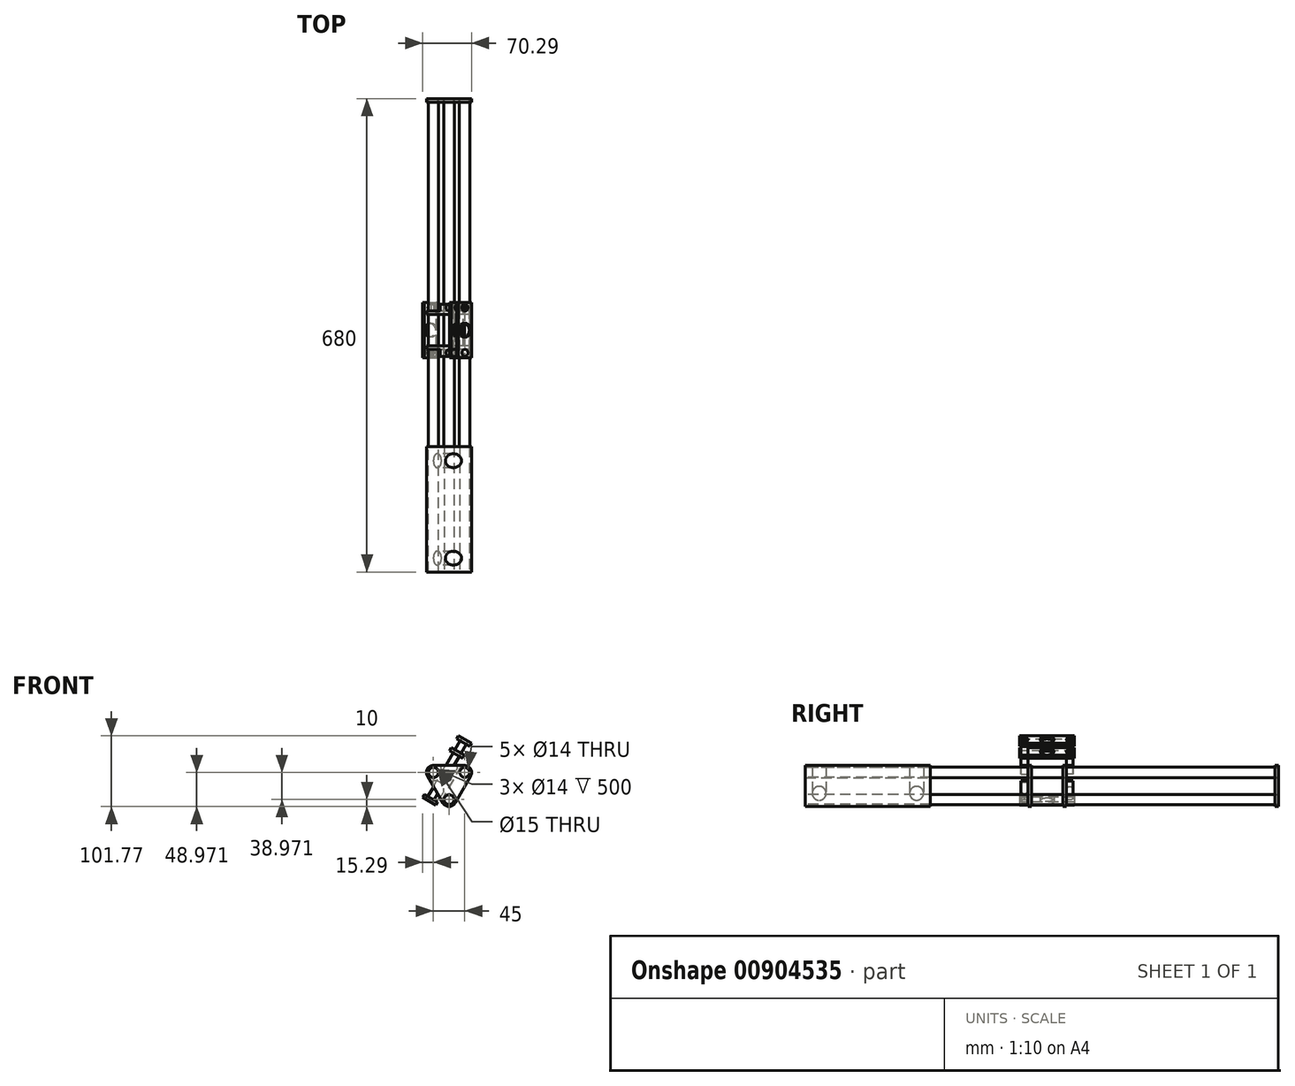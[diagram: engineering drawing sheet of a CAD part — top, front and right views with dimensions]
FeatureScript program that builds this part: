
annotation { "Feature Type Name" : "Feature", "Feature Type Description" : "" }
export const myFeature = defineFeature(function(context is Context, id is Id, definition is map)
    precondition{}
    {
        {
            var Q0;
            Q0=qCreatedBy(makeId("Front.planeOp"),FACE);
            var sketch = newSketch(context, id + "F0", { "sketchPlane" : qUnion([Q0])});
            skCircle(sketch, "E0", {"center": v(-22.5, 38.97) * mm, "radius": 7.5 * mm});
            skCircle(sketch, "E1", {"center": v(22.5, 38.97) * mm, "radius": 7.5 * mm});
            skCircle(sketch, "E2", {"center": v(0, 0) * mm, "radius": 7.5 * mm});
            skCircle(sketch, "E3", {"center": v(-22.5, 38.97) * mm, "radius": 7 * mm});
            skCircle(sketch, "E4", {"center": v(22.5, 38.97) * mm, "radius": 7 * mm});
            skCircle(sketch, "E5", {"center": v(0, 0) * mm, "radius": 7 * mm});
            skSolve(sketch);
        }
        {
            var Q0;
            Q0=makeQuery(id+"F0.imprint","IMPRINT",FACE,{"disambiguationData":[TD([[makeQuery(id+"F0.imprint","IMPRINT",EDGE,{"derivedFrom":sQuery(id+"F0.wireOp",EDGE,"E0")}),1.0]])]});
            var Q1;
            Q1=makeQuery(id+"F0.imprint","IMPRINT",FACE,{"disambiguationData":[TD([[makeQuery(id+"F0.imprint","IMPRINT",EDGE,{"derivedFrom":sQuery(id+"F0.wireOp",EDGE,"E1")}),1.0]])]});
            var Q2;
            Q2=makeQuery(id+"F0.imprint","IMPRINT",FACE,{"disambiguationData":[TD([[makeQuery(id+"F0.imprint","IMPRINT",EDGE,{"derivedFrom":sQuery(id+"F0.wireOp",EDGE,"E2")}),1.0]])]});
            extrude(context, id + "F1", {"entities" : qUnion([Q0, Q1, Q2]), "depth" : 500 * mm, "offsetDistance" : 25 * mm});
        }
        {
            var Q0;
            Q0=qCreatedBy(makeId("Front.planeOp"),FACE);
            var sketch = newSketch(context, id + "F2", { "sketchPlane" : qUnion([Q0])});
            skLineSegment(sketch, "E6", {"start": v(22.5, 48.97) * mm, "end": v(-22.5, 48.97) * mm});
            skArc(sketch, "E7", {"start": v(-22.5, 48.97) * mm, "mid": v(-31.16, 43.97) * mm, "end": v(-31.16, 33.97) * mm});
            skArc(sketch, "E8", {"start": v(31.16, 33.97) * mm, "mid": v(31.16, 43.97) * mm, "end": v(22.5, 48.97) * mm});
            skLineSegment(sketch, "E9", {"start": v(31.16, 33.97) * mm, "end": v(8.66, -5) * mm});
            skArc(sketch, "E10", {"start": v(-8.66, -5) * mm, "mid": v(0, -10) * mm, "end": v(8.66, -5) * mm});
            skLineSegment(sketch, "E11", {"start": v(-31.16, 33.97) * mm, "end": v(-8.66, -5) * mm});
            skSolve(sketch);
        }
        {
            var Q0;
            Q0=makeQuery(id+"F2.imprint","IMPRINT",FACE,{"disambiguationData":[TD([[makeQuery(id+"F2.imprint","IMPRINT",EDGE,{"derivedFrom":sQuery(id+"F2.wireOp",EDGE,"E6")}),1.0]])]});
            extrude(context, id + "F3", {"entities" : qUnion([Q0]), "depth" : 5 * mm, "offsetDistance" : 25 * mm});
        }
        {
            var Q0;
            Q0=makeQuery(id+"F1.opExtrude","CAP_FACE",FACE,{"disambiguationData":[OSD([sQuery(id+"F0.wireOp",EDGE,"E0"),sQuery(id+"F0.wireOp",EDGE,"E3")])],"isStart":false});
            var sketch = newSketch(context, id + "F4", { "sketchPlane" : qUnion([Q0])});
            skLineSegment(sketch, "E12", {"start": v(-22.5, 48.97) * mm, "end": v(22.5, 48.97) * mm});
            skArc(sketch, "E13", {"start": v(-22.5, 48.97) * mm, "mid": v(-31.16, 43.97) * mm, "end": v(-31.16, 33.97) * mm});
            skArc(sketch, "E14", {"start": v(31.16, 33.97) * mm, "mid": v(31.16, 43.97) * mm, "end": v(22.5, 48.97) * mm});
            skArc(sketch, "E15", {"start": v(-8.66, -5) * mm, "mid": v(0, -10) * mm, "end": v(8.66, -5) * mm});
            skLineSegment(sketch, "E16", {"start": v(-31.16, 33.97) * mm, "end": v(-8.66, -5) * mm});
            skLineSegment(sketch, "E17", {"start": v(31.16, 33.97) * mm, "end": v(8.66, -5) * mm});
            skSolve(sketch);
        }
        {
            var Q0;
            Q0=makeQuery(id+"F4.imprint","IMPRINT",FACE,{"disambiguationData":[TD([[makeQuery(id+"F4.imprint","IMPRINT",EDGE,{"derivedFrom":sQuery(id+"F4.wireOp",EDGE,"E12")}),-1.0]])]});
            extrude(context, id + "F5", {"entities" : qUnion([Q0]), "depth" : 180 * mm, "offsetDistance" : 25 * mm});
        }
        {
            var Q0;
            Q0=makeQuery(id+"F5.opExtrude","SWEPT_EDGE",EDGE,{"disambiguationData":[OSD([sQuery(id+"F4.wireOp",EDGE,"E15"),sQuery(id+"F4.wireOp",EDGE,"E16")])]});
            cPlane(context, id + "F6", {"entities" : qUnion([Q0]), "cplaneType" : CPlaneType.LINE_ANGLE, "offset" : 25 * mm, "angle" : 30 * degree, "width" : 150 * mm, "height" : 150 * mm});
        }
        {
            var Q0;
            Q0=qCreatedBy(id+"F6.planeOp",FACE);
            var sketch = newSketch(context, id + "F7", { "sketchPlane" : qUnion([Q0])});
            skCircle(sketch, "E18", {"center": v(-18.97, -660) * mm, "radius": 10 * mm});
            skCircle(sketch, "E19", {"center": v(-18.97, -520) * mm, "radius": 10 * mm});
            skSolve(sketch);
        }
        {
            var Q0;
            Q0=makeQuery(id+"F3.opExtrude","CAP_FACE",FACE,{"disambiguationData":[OSD([sQuery(id+"F2.wireOp",EDGE,"E6"),sQuery(id+"F2.wireOp",EDGE,"E7"),sQuery(id+"F2.wireOp",EDGE,"E8"),sQuery(id+"F2.wireOp",EDGE,"E9"),sQuery(id+"F2.wireOp",EDGE,"E10"),sQuery(id+"F2.wireOp",EDGE,"E11")])],"isStart":true});
            var sketch = newSketch(context, id + "F8", { "sketchPlane" : qUnion([Q0])});
            skCircle(sketch, "E20", {"center": v(-22.5, 38.97) * mm, "radius": 7 * mm});
            skCircle(sketch, "E21", {"center": v(22.5, 38.97) * mm, "radius": 7 * mm});
            skCircle(sketch, "E22", {"center": v(0, 0) * mm, "radius": 7 * mm});
            skSolve(sketch);
        }
        {
            var Q0;
            Q0=makeQuery(id+"F8.imprint","IMPRINT",FACE,{"disambiguationData":[TD([[makeQuery(id+"F8.imprint","IMPRINT",EDGE,{"derivedFrom":sQuery(id+"F8.wireOp",EDGE,"E20")}),1.0]])]});
            var Q1;
            Q1=makeQuery(id+"F8.imprint","IMPRINT",FACE,{"disambiguationData":[TD([[makeQuery(id+"F8.imprint","IMPRINT",EDGE,{"derivedFrom":sQuery(id+"F8.wireOp",EDGE,"E21")}),1.0]])]});
            var Q2;
            Q2=makeQuery(id+"F8.imprint","IMPRINT",FACE,{"disambiguationData":[TD([[makeQuery(id+"F8.imprint","IMPRINT",EDGE,{"derivedFrom":sQuery(id+"F8.wireOp",EDGE,"E22")}),1.0]])]});
            extrude(context, id + "F9", {"entities" : qUnion([Q0, Q1, Q2]), "operationType" : NewBodyOperationType.REMOVE, "oppositeDirection" : true, "depth" : 25 * mm, "offsetDistance" : 25 * mm});
        }
        {
            var Q0;
            Q0=makeQuery(id+"F5.opExtrude","CAP_FACE",FACE,{"disambiguationData":[OSD([sQuery(id+"F0.wireOp",EDGE,"E0"),sQuery(id+"F4.wireOp",EDGE,"E12"),sQuery(id+"F4.wireOp",EDGE,"E13"),sQuery(id+"F4.wireOp",EDGE,"E14"),sQuery(id+"F4.wireOp",EDGE,"E15"),sQuery(id+"F4.wireOp",EDGE,"E16"),sQuery(id+"F4.wireOp",EDGE,"E17")])],"isStart":false});
            var sketch = newSketch(context, id + "F10", { "sketchPlane" : qUnion([Q0])});
            skSolve(sketch);
        }
        {
            var Q0;
            Q0=makeQuery(id+"F10.imprint","IMPRINT",FACE,{"disambiguationData":[TD([[makeQuery(id+"F10.imprint","IMPRINT",EDGE,{"derivedFrom":makeQuery(id+"F5.opExtrude","CAP_EDGE",EDGE,{"disambiguationData":[OSD([sQuery(id+"F4.wireOp",EDGE,"E12")])],"isStart":false})}),-1.0]])]});
            var sketch = newSketch(context, id + "F11", { "sketchPlane" : qUnion([Q0])});
            skCircle(sketch, "E23", {"center": v(22.5, 38.97) * mm, "radius": 7 * mm});
            skCircle(sketch, "E24", {"center": v(0, 0) * mm, "radius": 7 * mm});
            skCircle(sketch, "E25", {"center": v(-22.5, 38.97) * mm, "radius": 7 * mm});
            skSolve(sketch);
        }
        {
            var Q0;
            Q0=makeQuery(id+"F11.imprint","IMPRINT",FACE,{"disambiguationData":[TD([[makeQuery(id+"F11.imprint","IMPRINT",EDGE,{"derivedFrom":sQuery(id+"F11.wireOp",EDGE,"E23")}),1.0]])]});
            var Q1;
            Q1=makeQuery(id+"F11.imprint","IMPRINT",FACE,{"disambiguationData":[TD([[makeQuery(id+"F11.imprint","IMPRINT",EDGE,{"derivedFrom":sQuery(id+"F11.wireOp",EDGE,"E24")}),1.0]])]});
            var Q2;
            Q2=makeQuery(id+"F11.imprint","IMPRINT",FACE,{"disambiguationData":[TD([[makeQuery(id+"F11.imprint","IMPRINT",EDGE,{"derivedFrom":sQuery(id+"F11.wireOp",EDGE,"E25")}),1.0]])]});
            extrude(context, id + "F12", {"entities" : qUnion([Q0, Q1, Q2]), "operationType" : NewBodyOperationType.REMOVE, "oppositeDirection" : true, "depth" : 195.3 * mm, "offsetDistance" : 25 * mm});
        }
        {
            var Q0;
            Q0=makeQuery(id+"F3.opExtrude","CAP_FACE",FACE,{"disambiguationData":[OSD([sQuery(id+"F2.wireOp",EDGE,"E6"),sQuery(id+"F2.wireOp",EDGE,"E7"),sQuery(id+"F2.wireOp",EDGE,"E8"),sQuery(id+"F2.wireOp",EDGE,"E9"),sQuery(id+"F2.wireOp",EDGE,"E10"),sQuery(id+"F2.wireOp",EDGE,"E11")])],"isStart":false});
            cPlane(context, id + "F13", {"entities" : qUnion([Q0]), "cplaneType" : CPlaneType.OFFSET, "offset" : 300 * mm, "width" : 150 * mm, "height" : 150 * mm});
        }
        {
            var Q0;
            Q0=qCreatedBy(id+"F13.planeOp",FACE);
            var sketch = newSketch(context, id + "F14", { "sketchPlane" : qUnion([Q0])});
            skLineSegment(sketch, "E26", {"start": v(22.5, 48.97) * mm, "end": v(-22.5, 48.97) * mm});
            skArc(sketch, "E27", {"start": v(-22.5, 48.97) * mm, "mid": v(-31.16, 43.97) * mm, "end": v(-31.16, 33.97) * mm});
            skArc(sketch, "E28", {"start": v(31.16, 33.97) * mm, "mid": v(31.16, 43.97) * mm, "end": v(22.5, 48.97) * mm});
            skLineSegment(sketch, "E29", {"start": v(31.16, 33.97) * mm, "end": v(8.66, -5) * mm});
            skArc(sketch, "E30", {"start": v(-8.66, -5) * mm, "mid": v(0, -10) * mm, "end": v(8.66, -5) * mm});
            skLineSegment(sketch, "E31", {"start": v(-31.16, 33.97) * mm, "end": v(-8.66, -5) * mm});
            skSolve(sketch);
        }
        {
            var Q0;
            Q0=makeQuery(id+"F14.imprint","IMPRINT",FACE,{"disambiguationData":[TD([[makeQuery(id+"F14.imprint","IMPRINT",EDGE,{"derivedFrom":sQuery(id+"F14.wireOp",EDGE,"E26")}),1.0]])]});
            extrude(context, id + "F15", {"entities" : qUnion([Q0]), "depth" : 5 * mm, "offsetDistance" : 25 * mm});
        }
        {
            var Q0;
            Q0=makeQuery(id+"F3.opExtrude","CAP_FACE",FACE,{"disambiguationData":[OSD([sQuery(id+"F2.wireOp",EDGE,"E6"),sQuery(id+"F2.wireOp",EDGE,"E7"),sQuery(id+"F2.wireOp",EDGE,"E8"),sQuery(id+"F2.wireOp",EDGE,"E9"),sQuery(id+"F2.wireOp",EDGE,"E10"),sQuery(id+"F2.wireOp",EDGE,"E11")])],"isStart":false});
            cPlane(context, id + "F16", {"entities" : qUnion([Q0]), "cplaneType" : CPlaneType.OFFSET, "offset" : 350 * mm, "width" : 150 * mm, "height" : 150 * mm});
        }
        {
            var Q0;
            Q0=qCreatedBy(id+"F16.planeOp",FACE);
            var sketch = newSketch(context, id + "F17", { "sketchPlane" : qUnion([Q0])});
            skLineSegment(sketch, "E32", {"start": v(22.5, 48.97) * mm, "end": v(-22.5, 48.97) * mm});
            skArc(sketch, "E33", {"start": v(-22.5, 48.97) * mm, "mid": v(-31.16, 43.97) * mm, "end": v(-31.16, 33.97) * mm});
            skArc(sketch, "E34", {"start": v(31.16, 33.97) * mm, "mid": v(31.16, 43.97) * mm, "end": v(22.5, 48.97) * mm});
            skLineSegment(sketch, "E35", {"start": v(31.16, 33.97) * mm, "end": v(8.66, -5) * mm});
            skArc(sketch, "E36", {"start": v(-8.66, -5) * mm, "mid": v(0, -10) * mm, "end": v(8.66, -5) * mm});
            skLineSegment(sketch, "E37", {"start": v(-31.16, 33.97) * mm, "end": v(-8.66, -5) * mm});
            skSolve(sketch);
        }
        {
            var Q0;
            Q0=makeQuery(id+"F17.imprint","IMPRINT",FACE,{"disambiguationData":[TD([[makeQuery(id+"F17.imprint","IMPRINT",EDGE,{"derivedFrom":sQuery(id+"F17.wireOp",EDGE,"E32")}),1.0]])]});
            extrude(context, id + "F18", {"entities" : qUnion([Q0]), "depth" : 5 * mm, "offsetDistance" : 25 * mm});
        }
        {
            var Q0;
            Q0=makeQuery(id+"F15.opExtrude","CAP_FACE",FACE,{"disambiguationData":[OSD([sQuery(id+"F14.wireOp",EDGE,"E26"),sQuery(id+"F14.wireOp",EDGE,"E27"),sQuery(id+"F14.wireOp",EDGE,"E28"),sQuery(id+"F14.wireOp",EDGE,"E29"),sQuery(id+"F14.wireOp",EDGE,"E30"),sQuery(id+"F14.wireOp",EDGE,"E31")])],"isStart":true});
            var sketch = newSketch(context, id + "F19", { "sketchPlane" : qUnion([Q0])});
            skLineSegment(sketch, "E38", {"start": v(12.5, 48.97) * mm, "end": v(-12.5, 48.97) * mm});
            skArc(sketch, "E39", {"start": v(-12.5, 48.97) * mm, "mid": v(0, 36.47) * mm, "end": v(12.5, 48.97) * mm});
            skSolve(sketch);
        }
        {
            var Q0;
            Q0=qSketchRegion(id+"F19",true);
            extrude(context, id + "F20", {"entities" : qUnion([Q0]), "operationType" : NewBodyOperationType.ADD, "depth" : 10 * mm, "offsetDistance" : 25 * mm});
        }
        {
            var Q0;
            Q0=makeQuery(id+"F18.opExtrude","CAP_FACE",FACE,{"disambiguationData":[OSD([sQuery(id+"F17.wireOp",EDGE,"E32"),sQuery(id+"F17.wireOp",EDGE,"E33"),sQuery(id+"F17.wireOp",EDGE,"E34"),sQuery(id+"F17.wireOp",EDGE,"E35"),sQuery(id+"F17.wireOp",EDGE,"E36"),sQuery(id+"F17.wireOp",EDGE,"E37")])],"isStart":false});
            var sketch = newSketch(context, id + "F21", { "sketchPlane" : qUnion([Q0])});
            skLineSegment(sketch, "E40", {"start": v(-12.5, 48.97) * mm, "end": v(12.5, 48.97) * mm});
            skArc(sketch, "E41", {"start": v(-12.5, 48.97) * mm, "mid": v(0, 36.47) * mm, "end": v(12.5, 48.97) * mm});
            skSolve(sketch);
        }
        {
            var Q0;
            Q0=qSketchRegion(id+"F21",true);
            extrude(context, id + "F22", {"entities" : qUnion([Q0]), "operationType" : NewBodyOperationType.ADD, "depth" : 10 * mm, "offsetDistance" : 25 * mm});
        }
        {
            var Q0;
            {var subQ0=sQuery(id+"F19.wireOp",EDGE,"E39");var subQ1=sQuery(id+"F19.wireOp",EDGE,"E38");var subQ2=sQuery(id+"F14.wireOp",EDGE,"E26");Q0=makeQuery(id+"F20.opExtrude","SWEPT_EDGE",EDGE,{"disambiguationData":[OSD([subQ2,subQ1,subQ0]),TDD([makeQuery(id+"F19.imprint","INTERSECT",VERTEX,{"disambiguationData":[OD(1.0)],"derivedFrom":[makeQuery(id+"F15.opExtrude","CAP_EDGE",EDGE,{"disambiguationData":[OSD([subQ2])],"isStart":true}),subQ1,subQ0]})])]});}
            cPlane(context, id + "F23", {"entities" : qUnion([Q0]), "cplaneType" : CPlaneType.LINE_ANGLE, "offset" : 0 * mm, "angle" : 30 * degree, "oppositeDirection" : true, "width" : 150 * mm, "height" : 150 * mm});
        }
        {
            var Q0;
            Q0=qCreatedBy(id+"F23.planeOp",FACE);
            var sketch = newSketch(context, id + "F24", { "sketchPlane" : qUnion([Q0])});
            skCircle(sketch, "E42", {"center": v(-23.31, 300) * mm, "radius": 5 * mm});
            skSolve(sketch);
        }
        {
            var Q0;
            Q0=makeQuery(id+"F24.imprint","IMPRINT",FACE,{"disambiguationData":[TD([[makeQuery(id+"F24.imprint","IMPRINT",EDGE,{"derivedFrom":sQuery(id+"F24.wireOp",EDGE,"E42")}),1.0]])]});
            extrude(context, id + "F25", {"entities" : qUnion([Q0]), "operationType" : NewBodyOperationType.ADD, "oppositeDirection" : true, "depth" : 50 * mm, "offsetDistance" : 25 * mm});
        }
        {
            var Q0;
            {var subQ0=sQuery(id+"F21.wireOp",EDGE,"E41");var subQ1=sQuery(id+"F21.wireOp",EDGE,"E40");var subQ2=sQuery(id+"F17.wireOp",EDGE,"E32");Q0=makeQuery(id+"F22.opExtrude","SWEPT_EDGE",EDGE,{"disambiguationData":[OSD([subQ2,subQ1,subQ0]),TDD([makeQuery(id+"F21.imprint","INTERSECT",VERTEX,{"disambiguationData":[OD(1.0)],"derivedFrom":[makeQuery(id+"F18.opExtrude","CAP_EDGE",EDGE,{"disambiguationData":[OSD([subQ2])],"isStart":false}),subQ1,subQ0]})])]});}
            cPlane(context, id + "F26", {"entities" : qUnion([Q0]), "cplaneType" : CPlaneType.LINE_ANGLE, "offset" : 25 * mm, "angle" : 30 * degree, "width" : 150 * mm, "height" : 150 * mm});
        }
        {
            var Q0;
            Q0=qCreatedBy(id+"F26.planeOp",FACE);
            var sketch = newSketch(context, id + "F27", { "sketchPlane" : qUnion([Q0])});
            skCircle(sketch, "E43", {"center": v(-23.31, -365) * mm, "radius": 5 * mm});
            skSolve(sketch);
        }
        {
            var Q0;
            Q0=qSketchRegion(id+"F27",true);
            extrude(context, id + "F28", {"entities" : qUnion([Q0]), "operationType" : NewBodyOperationType.ADD, "depth" : 50 * mm, "offsetDistance" : 25 * mm});
        }
        {
            var Q0;
            Q0=makeQuery(id+"F28.opExtrude","CAP_FACE",FACE,{"disambiguationData":[OSD([sQuery(id+"F27.wireOp",EDGE,"E43")])],"isStart":false});
            var sketch = newSketch(context, id + "F29", { "sketchPlane" : qUnion([Q0])});
            skLineSegment(sketch, "E44.bottom", {"start": v(-34.31, -372) * mm, "end": v(-12.31, -372) * mm});
            skLineSegment(sketch, "E44.top", {"start": v(-34.31, -293) * mm, "end": v(-12.31, -293) * mm});
            skLineSegment(sketch, "E44.left", {"start": v(-34.31, -372) * mm, "end": v(-34.31, -293) * mm});
            skLineSegment(sketch, "E44.right", {"start": v(-12.31, -372) * mm, "end": v(-12.31, -293) * mm});
            skSolve(sketch);
        }
        {
            var Q0;
            Q0=qSketchRegion(id+"F29",true);
            extrude(context, id + "F30", {"entities" : qUnion([Q0]), "oppositeDirection" : true, "depth" : 5 * mm, "offsetDistance" : 25 * mm});
        }
        {
            var Q0;
            Q0=makeQuery(id+"F30.opExtrude","CAP_FACE",FACE,{"disambiguationData":[OSD([sQuery(id+"F29.wireOp",EDGE,"E44.bottom"),sQuery(id+"F29.wireOp",EDGE,"E44.top"),sQuery(id+"F29.wireOp",EDGE,"E44.left"),sQuery(id+"F29.wireOp",EDGE,"E44.right")])],"isStart":true});
            var sketch = newSketch(context, id + "F31", { "sketchPlane" : qUnion([Q0])});
            skCircle(sketch, "E45", {"center": v(-23.31, -332.5) * mm, "radius": 10 * mm});
            skSolve(sketch);
        }
        {
            var Q0;
            Q0=makeQuery(id+"F31.imprint","IMPRINT",FACE,{"disambiguationData":[TD([[makeQuery(id+"F31.imprint","IMPRINT",EDGE,{"derivedFrom":sQuery(id+"F31.wireOp",EDGE,"E45")}),1.0]])]});
            extrude(context, id + "F32", {"entities" : qUnion([Q0]), "operationType" : NewBodyOperationType.REMOVE, "oppositeDirection" : true, "depth" : 28.9 * mm, "offsetDistance" : 25 * mm});
        }
        {
            var Q0;
            Q0=makeQuery(id+"F30.opExtrude","CAP_FACE",FACE,{"disambiguationData":[OSD([sQuery(id+"F29.wireOp",EDGE,"E44.bottom"),sQuery(id+"F29.wireOp",EDGE,"E44.top"),sQuery(id+"F29.wireOp",EDGE,"E44.left"),sQuery(id+"F29.wireOp",EDGE,"E44.right")])],"isStart":false});
            cPlane(context, id + "F33", {"entities" : qUnion([Q0]), "cplaneType" : CPlaneType.OFFSET, "offset" : 15 * mm, "width" : 150 * mm, "height" : 150 * mm});
        }
        {
            var Q0;
            Q0=qCreatedBy(id+"F33.planeOp",FACE);
            var sketch = newSketch(context, id + "F34", { "sketchPlane" : qUnion([Q0])});
            skLineSegment(sketch, "E46.bottom", {"start": v(-34.31, 293) * mm, "end": v(-12.31, 293) * mm});
            skLineSegment(sketch, "E46.top", {"start": v(-34.31, 372) * mm, "end": v(-12.31, 372) * mm});
            skLineSegment(sketch, "E46.left", {"start": v(-34.31, 293) * mm, "end": v(-34.31, 372) * mm});
            skLineSegment(sketch, "E46.right", {"start": v(-12.31, 293) * mm, "end": v(-12.31, 372) * mm});
            skSolve(sketch);
        }
        {
            var Q0;
            Q0=makeQuery(id+"F34.imprint","IMPRINT",FACE,{"disambiguationData":[TD([[makeQuery(id+"F34.imprint","IMPRINT",EDGE,{"derivedFrom":sQuery(id+"F34.wireOp",EDGE,"E46.bottom")}),1.0]])]});
            extrude(context, id + "F35", {"entities" : qUnion([Q0]), "depth" : 5 * mm, "offsetDistance" : 25 * mm});
        }
        {
            var Q0;
            Q0=makeQuery(id+"F35.opExtrude","CAP_FACE",FACE,{"disambiguationData":[OSD([sQuery(id+"F34.wireOp",EDGE,"E46.bottom"),sQuery(id+"F34.wireOp",EDGE,"E46.top"),sQuery(id+"F34.wireOp",EDGE,"E46.left"),sQuery(id+"F34.wireOp",EDGE,"E46.right")])],"isStart":true});
            var sketch = newSketch(context, id + "F36", { "sketchPlane" : qUnion([Q0])});
            skCircle(sketch, "E47", {"center": v(-23.31, -332.5) * mm, "radius": 10 * mm});
            skSolve(sketch);
        }
        {
            var Q0;
            Q0=makeQuery(id+"F36.imprint","IMPRINT",FACE,{"disambiguationData":[TD([[makeQuery(id+"F36.imprint","IMPRINT",EDGE,{"derivedFrom":sQuery(id+"F36.wireOp",EDGE,"E47")}),1.0]])]});
            extrude(context, id + "F37", {"entities" : qUnion([Q0]), "operationType" : NewBodyOperationType.REMOVE, "oppositeDirection" : true, "depth" : 14.6 * mm, "offsetDistance" : 25 * mm});
        }
        {
            var Q0;
            Q0=makeQuery(id+"F15.opExtrude","CAP_FACE",FACE,{"disambiguationData":[OSD([sQuery(id+"F14.wireOp",EDGE,"E26"),sQuery(id+"F14.wireOp",EDGE,"E27"),sQuery(id+"F14.wireOp",EDGE,"E28"),sQuery(id+"F14.wireOp",EDGE,"E29"),sQuery(id+"F14.wireOp",EDGE,"E30"),sQuery(id+"F14.wireOp",EDGE,"E31")])],"isStart":true});
            var sketch = newSketch(context, id + "F38", { "sketchPlane" : qUnion([Q0])});
            skLineSegment(sketch, "E48", {"start": v(26.16, 25.31) * mm, "end": v(13.66, 3.66) * mm});
            skArc(sketch, "E49", {"start": v(26.16, 25.31) * mm, "mid": v(9.08, 20.74) * mm, "end": v(13.66, 3.66) * mm});
            skSolve(sketch);
        }
        {
            var Q0;
            Q0=makeQuery(id+"F38.imprint","IMPRINT",FACE,{"disambiguationData":[TD([[makeQuery(id+"F38.imprint","IMPRINT",EDGE,{"derivedFrom":sQuery(id+"F38.wireOp",EDGE,"E48")}),-1.0]])]});
            extrude(context, id + "F39", {"entities" : qUnion([Q0]), "operationType" : NewBodyOperationType.ADD, "depth" : 10 * mm, "offsetDistance" : 25 * mm});
        }
        {
            var Q0;
            Q0=makeQuery(id+"F18.opExtrude","CAP_FACE",FACE,{"disambiguationData":[OSD([sQuery(id+"F17.wireOp",EDGE,"E32"),sQuery(id+"F17.wireOp",EDGE,"E33"),sQuery(id+"F17.wireOp",EDGE,"E34"),sQuery(id+"F17.wireOp",EDGE,"E35"),sQuery(id+"F17.wireOp",EDGE,"E36"),sQuery(id+"F17.wireOp",EDGE,"E37")])],"isStart":false});
            var sketch = newSketch(context, id + "F40", { "sketchPlane" : qUnion([Q0])});
            skLineSegment(sketch, "E50", {"start": v(-26.16, 25.31) * mm, "end": v(-13.66, 3.66) * mm});
            skArc(sketch, "E51", {"start": v(-13.66, 3.66) * mm, "mid": v(-9.08, 20.74) * mm, "end": v(-26.16, 25.31) * mm});
            skSolve(sketch);
        }
        {
            var Q0;
            Q0=makeQuery(id+"F40.imprint","IMPRINT",FACE,{"disambiguationData":[TD([[makeQuery(id+"F40.imprint","IMPRINT",EDGE,{"derivedFrom":sQuery(id+"F40.wireOp",EDGE,"E50")}),1.0]])]});
            extrude(context, id + "F41", {"entities" : qUnion([Q0]), "operationType" : NewBodyOperationType.ADD, "depth" : 10 * mm, "offsetDistance" : 25 * mm});
        }
        {
            var Q0;
            {var subQ0=sQuery(id+"F38.wireOp",EDGE,"E49");var subQ1=sQuery(id+"F38.wireOp",EDGE,"E48");var subQ2=sQuery(id+"F14.wireOp",EDGE,"E31");Q0=makeQuery(id+"F39.opExtrude","SWEPT_EDGE",EDGE,{"disambiguationData":[OSD([subQ2,subQ1,subQ0]),TDD([makeQuery(id+"F38.imprint","INTERSECT",VERTEX,{"disambiguationData":[OD(0.0)],"derivedFrom":[makeQuery(id+"F15.opExtrude","CAP_EDGE",EDGE,{"disambiguationData":[OSD([subQ2])],"isStart":true}),subQ1,subQ0]})])]});}
            cPlane(context, id + "F42", {"entities" : qUnion([Q0]), "cplaneType" : CPlaneType.LINE_ANGLE, "offset" : 25 * mm, "angle" : 30 * degree, "oppositeDirection" : true, "width" : 150 * mm, "height" : 150 * mm});
        }
        {
            var Q0;
            {var subQ0=sQuery(id+"F40.wireOp",EDGE,"E51");var subQ1=sQuery(id+"F40.wireOp",EDGE,"E50");var subQ2=sQuery(id+"F17.wireOp",EDGE,"E37");Q0=makeQuery(id+"F41.opExtrude","SWEPT_EDGE",EDGE,{"disambiguationData":[OSD([subQ2,subQ1,subQ0]),TDD([makeQuery(id+"F40.imprint","INTERSECT",VERTEX,{"disambiguationData":[OD(0.0)],"derivedFrom":[makeQuery(id+"F18.opExtrude","CAP_EDGE",EDGE,{"disambiguationData":[OSD([subQ2])],"isStart":false}),subQ1,subQ0]})])]});}
            cPlane(context, id + "F43", {"entities" : qUnion([Q0]), "cplaneType" : CPlaneType.LINE_ANGLE, "offset" : 25 * mm, "angle" : 30 * degree, "width" : 150 * mm, "height" : 150 * mm});
        }
        {
            var Q0;
            Q0=qCreatedBy(id+"F42.planeOp",FACE);
            var sketch = newSketch(context, id + "F44", { "sketchPlane" : qUnion([Q0])});
            skCircle(sketch, "E52", {"center": v(-23.31, 300) * mm, "radius": 5 * mm});
            skSolve(sketch);
        }
        {
            var Q0;
            Q0=qSketchRegion(id+"F44",true);
            extrude(context, id + "F45", {"entities" : qUnion([Q0]), "operationType" : NewBodyOperationType.ADD, "depth" : 25 * mm, "offsetDistance" : 25 * mm});
        }
        {
            var Q0;
            Q0=qCreatedBy(id+"F43.planeOp",FACE);
            var sketch = newSketch(context, id + "F46", { "sketchPlane" : qUnion([Q0])});
            skCircle(sketch, "E53", {"center": v(-23.31, -365) * mm, "radius": 5 * mm});
            skSolve(sketch);
        }
        {
            var Q0;
            Q0=qSketchRegion(id+"F46",true);
            extrude(context, id + "F47", {"entities" : qUnion([Q0]), "operationType" : NewBodyOperationType.ADD, "oppositeDirection" : true, "depth" : 25.1 * mm, "offsetDistance" : 25 * mm});
        }
        {
            var Q0;
            Q0=makeQuery(id+"F45.opExtrude","CAP_FACE",FACE,{"disambiguationData":[OSD([sQuery(id+"F44.wireOp",EDGE,"E52")])],"isStart":false});
            var sketch = newSketch(context, id + "F48", { "sketchPlane" : qUnion([Q0])});
            skLineSegment(sketch, "E54.bottom", {"start": v(-34.31, 293) * mm, "end": v(-12.31, 293) * mm});
            skLineSegment(sketch, "E54.top", {"start": v(-34.31, 372) * mm, "end": v(-12.31, 372) * mm});
            skLineSegment(sketch, "E54.left", {"start": v(-34.31, 293) * mm, "end": v(-34.31, 372) * mm});
            skLineSegment(sketch, "E54.right", {"start": v(-12.31, 293) * mm, "end": v(-12.31, 372) * mm});
            skSolve(sketch);
        }
        {
            var Q0;
            Q0=makeQuery(id+"F48.imprint","IMPRINT",FACE,{"disambiguationData":[TD([[makeQuery(id+"F48.imprint","IMPRINT",EDGE,{"derivedFrom":sQuery(id+"F48.wireOp",EDGE,"E54.bottom")}),1.0]])]});
            extrude(context, id + "F49", {"entities" : qUnion([Q0]), "operationType" : NewBodyOperationType.ADD, "oppositeDirection" : true, "depth" : 5 * mm, "offsetDistance" : 25 * mm});
        }
        {
            var Q0;
            Q0=makeQuery(id+"F49.opExtrude","CAP_FACE",FACE,{"disambiguationData":[OSD([sQuery(id+"F44.wireOp",EDGE,"E52"),sQuery(id+"F48.wireOp",EDGE,"E54.bottom"),sQuery(id+"F48.wireOp",EDGE,"E54.top"),sQuery(id+"F48.wireOp",EDGE,"E54.left"),sQuery(id+"F48.wireOp",EDGE,"E54.right")])],"isStart":true});
            var sketch = newSketch(context, id + "F50", { "sketchPlane" : qUnion([Q0])});
            skCircle(sketch, "E55", {"center": v(-23.31, 332.5) * mm, "radius": 10 * mm});
            skSolve(sketch);
        }
        {
            var Q0;
            Q0=makeQuery(id+"F50.imprint","IMPRINT",FACE,{"disambiguationData":[TD([[makeQuery(id+"F50.imprint","IMPRINT",EDGE,{"derivedFrom":sQuery(id+"F50.wireOp",EDGE,"E55")}),1.0]])]});
            extrude(context, id + "F51", {"entities" : qUnion([Q0]), "operationType" : NewBodyOperationType.REMOVE, "oppositeDirection" : true, "depth" : 25 * mm, "offsetDistance" : 25 * mm});
        }
        {
            var Q0;
            Q0=makeQuery(id+"F30.opExtrude","CAP_FACE",FACE,{"disambiguationData":[OSD([sQuery(id+"F29.wireOp",EDGE,"E44.bottom"),sQuery(id+"F29.wireOp",EDGE,"E44.top"),sQuery(id+"F29.wireOp",EDGE,"E44.left"),sQuery(id+"F29.wireOp",EDGE,"E44.right")])],"isStart":true});
            var sketch = newSketch(context, id + "F52", { "sketchPlane" : qUnion([Q0])});
            skCircle(sketch, "E56", {"center": v(-23.31, -300) * mm, "radius": 5 * mm});
            skSolve(sketch);
        }
        {
            var Q0;
            Q0=makeQuery(id+"F52.imprint","IMPRINT",FACE,{"disambiguationData":[TD([[makeQuery(id+"F52.imprint","IMPRINT",EDGE,{"derivedFrom":sQuery(id+"F52.wireOp",EDGE,"E56")}),1.0]])]});
            extrude(context, id + "F53", {"entities" : qUnion([Q0]), "operationType" : NewBodyOperationType.REMOVE, "oppositeDirection" : true, "depth" : 25 * mm, "offsetDistance" : 25 * mm});
        }
        {
            var Q0;
            Q0=makeQuery(id+"F35.opExtrude","CAP_FACE",FACE,{"disambiguationData":[OSD([sQuery(id+"F34.wireOp",EDGE,"E46.bottom"),sQuery(id+"F34.wireOp",EDGE,"E46.top"),sQuery(id+"F34.wireOp",EDGE,"E46.left"),sQuery(id+"F34.wireOp",EDGE,"E46.right")])],"isStart":true});
            var sketch = newSketch(context, id + "F54", { "sketchPlane" : qUnion([Q0])});
            skCircle(sketch, "E57", {"center": v(-23.31, -300) * mm, "radius": 5 * mm});
            skSolve(sketch);
        }
        {
            var Q0;
            Q0=qSketchRegion(id+"F54",true);
            extrude(context, id + "F55", {"entities" : qUnion([Q0]), "operationType" : NewBodyOperationType.REMOVE, "oppositeDirection" : true, "depth" : 5 * mm, "offsetDistance" : 25 * mm});
        }
        {
            var Q0;
            Q0=qSketchRegion(id+"F7",true);
            extrude(context, id + "F56", {"entities" : qUnion([Q0]), "operationType" : NewBodyOperationType.REMOVE, "depth" : 101 * mm, "offsetDistance" : 25 * mm});
        }
    });
